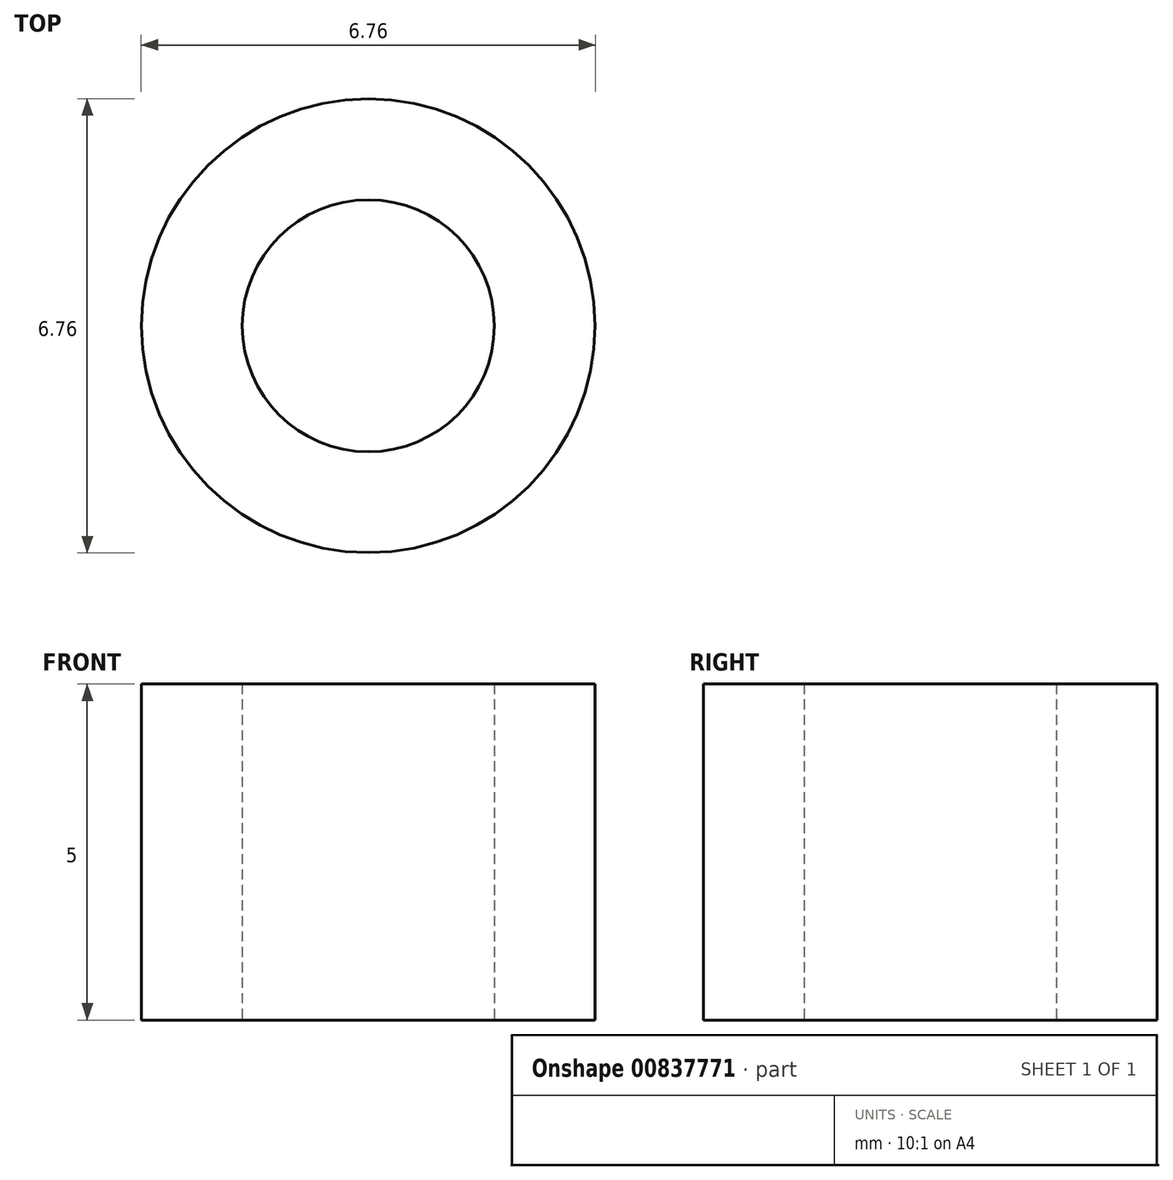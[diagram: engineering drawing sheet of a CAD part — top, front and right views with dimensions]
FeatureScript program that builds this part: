
annotation { "Feature Type Name" : "Feature", "Feature Type Description" : "" }
export const myFeature = defineFeature(function(context is Context, id is Id, definition is map)
    precondition{}
    {
        {
            var Q0;
            Q0=qCreatedBy(makeId("Top.planeOp"),FACE);
            var sketch = newSketch(context, id + "F0", { "sketchPlane" : qUnion([Q0])});
            skCircle(sketch, "E0", {"center": v(0, 0) * mm, "radius": 3.38 * mm});
            skCircle(sketch, "E1", {"center": v(0, 0) * mm, "radius": 1.88 * mm});
            skSolve(sketch);
        }
        {
            var Q0;
            Q0=makeQuery(id+"F0.imprint","IMPRINT",FACE,{"disambiguationData":[TD([[makeQuery(id+"F0.imprint","IMPRINT",EDGE,{"derivedFrom":sQuery(id+"F0.wireOp",EDGE,"E0")}),1.0]])]});
            extrude(context, id + "F1", {"entities" : qUnion([Q0]), "depth" : 5 * mm, "offsetDistance" : 25 * mm});
        }
    });
